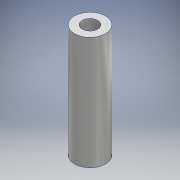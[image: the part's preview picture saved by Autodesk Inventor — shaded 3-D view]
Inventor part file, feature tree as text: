
AUTODESK INVENTOR PART (.ipt)
format: ipt  version: 2016 (Build 200138000, 138)  size: 114,688 bytes
history: native  units: mm
features: sketch x2, extrude x2, hole x2, other x1
ambient origin geometry x8: Origin, YZ Plane, XZ Plane, XY Plane, X Axis, Y Axis, Z Axis, Center Point
bodies: Body1 (feature_tree)
feature tree (7):
  other  "ソリッド1"
  sketch  "スケッチ1"
  extrude  "押し出し1"  Depth=6.0mm
  sketch  "スケッチ2"
  extrude  "押し出し2"  Depth=3.001mm
  hole  "穴1"  [1 undecoded]
  hole  "穴2"  [1 undecoded]
note: 2 required parameter values undecoded (feature->parameter linkage not recoverable at this tier; creation-order binding heuristic only, values carry confidence <= 0.55)
